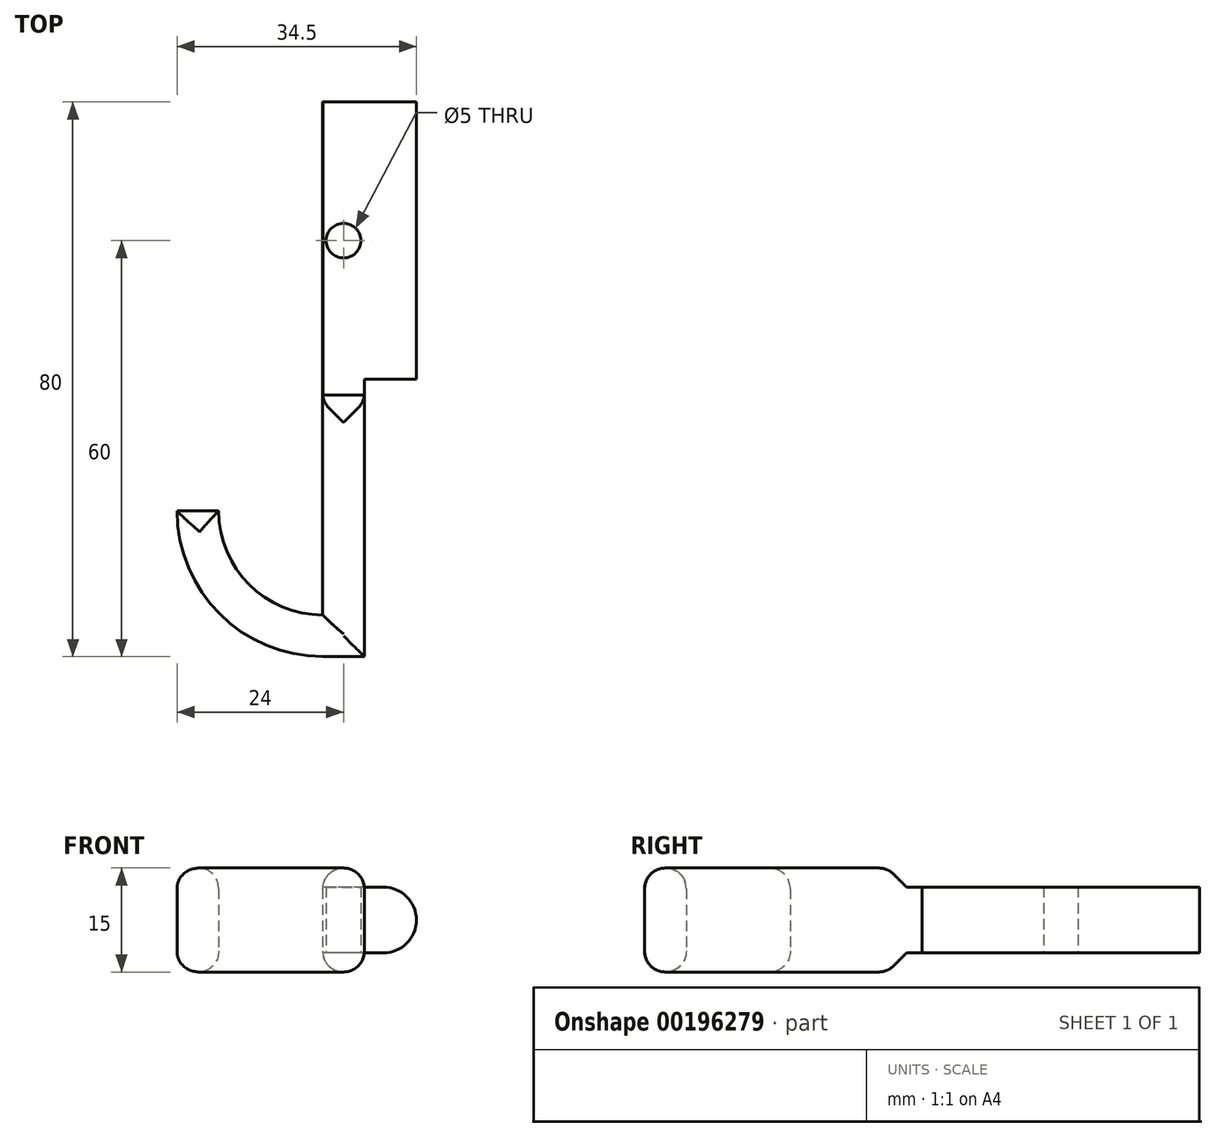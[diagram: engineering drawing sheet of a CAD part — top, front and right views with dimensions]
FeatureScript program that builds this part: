
annotation { "Feature Type Name" : "Feature", "Feature Type Description" : "" }
export const myFeature = defineFeature(function(context is Context, id is Id, definition is map)
    precondition{}
    {
        {
            var Q0;
            Q0=qCreatedBy(makeId("Top.planeOp"),FACE);
            var sketch = newSketch(context, id + "F0", { "sketchPlane" : qUnion([Q0])});
            skArc(sketch, "E0", {"start": v(0, -21) * mm, "mid": v(-14.85, -14.85) * mm, "end": v(-21, 0) * mm});
            skLineSegment(sketch, "E1", {"start": v(0, 0) * mm, "end": v(0, -15) * mm, "construction": true});
            skArc(sketch, "E2", {"start": v(0, -15) * mm, "mid": v(-10.6, -10.6) * mm, "end": v(-15, 0) * mm});
            skLineSegment(sketch, "E3", {"start": v(-21, 0) * mm, "end": v(-15, 0) * mm});
            skLineSegment(sketch, "E4", {"start": v(0, 0) * mm, "end": v(0, -21) * mm});
            skLineSegment(sketch, "E5.bottom", {"start": v(0, -21) * mm, "end": v(6, -21) * mm});
            skLineSegment(sketch, "E5.top", {"start": v(0, 19) * mm, "end": v(6, 19) * mm});
            skLineSegment(sketch, "E5.left", {"start": v(0, -21) * mm, "end": v(0, 19) * mm});
            skLineSegment(sketch, "E5.right", {"start": v(6, -21) * mm, "end": v(6, 19) * mm});
            skSolve(sketch);
        }
        {
            var Q0;
            Q0=qSketchRegion(id+"F0",true);
            extrude(context, id + "F1", {"entities" : qUnion([Q0]), "depth" : 15 * mm});
        }
        {
            var Q0;
            Q0=makeQuery(id+"F1.opExtrude","SWEPT_FACE",FACE,{"disambiguationData":[OSD([sQuery(id+"F0.wireOp",EDGE,"E5.top")])]});
            var sketch = newSketch(context, id + "F2", { "sketchPlane" : qUnion([Q0])});
            skLineSegment(sketch, "E6", {"start": v(-6, 15) * mm, "end": v(0, 0) * mm, "construction": true});
            skLineSegment(sketch, "E7", {"start": v(0, 0) * mm, "end": v(-6, 0) * mm, "construction": true});
            skLineSegment(sketch, "E8", {"start": v(-6, 0) * mm, "end": v(0, 15) * mm, "construction": true});
            skPoint(sketch, "E9", {"position": v(-3, 7.5) * mm});
            skLineSegment(sketch, "E10", {"start": v(-3, 7.5) * mm, "end": v(-3, 41.48) * mm, "construction": true});
            skLineSegment(sketch, "E11", {"start": v(-3, 7.5) * mm, "end": v(-3, -27.06) * mm, "construction": true});
            skLineSegment(sketch, "E12.bottom", {"start": v(-8.75, 2.75) * mm, "end": v(2.75, 2.75) * mm, "construction": true});
            skLineSegment(sketch, "E12.left", {"start": v(-8.75, 2.75) * mm, "end": v(-8.75, 12.25) * mm, "construction": true});
            skLineSegment(sketch, "E12.right", {"start": v(2.75, 2.75) * mm, "end": v(2.75, 12.25) * mm, "construction": true});
            skLineSegment(sketch, "E13", {"start": v(-3, 7.5) * mm, "end": v(-14.99, 7.5) * mm, "construction": true});
            skLineSegment(sketch, "E14", {"start": v(-14.99, 7.5) * mm, "end": v(-3, 7.5) * mm, "construction": true});
            skLineSegment(sketch, "E15", {"start": v(5.8, 7.5) * mm, "end": v(-3, 7.5) * mm, "construction": true});
            skPoint(sketch, "E16", {"position": v(-8.75, 7.5) * mm});
            skPoint(sketch, "E17", {"position": v(2.75, 7.5) * mm});
            skCircle(sketch, "E18", {"center": v(2.75, 7.5) * mm, "radius": 4.75 * mm, "construction": true});
            skCircle(sketch, "E19", {"center": v(-8.75, 7.5) * mm, "radius": 4.75 * mm, "construction": true});
            skLineSegment(sketch, "E20", {"start": v(2.75, 12.25) * mm, "end": v(-8.75, 12.25) * mm, "construction": true});
            skLineSegment(sketch, "E21", {"start": v(-8.75, 2.75) * mm, "end": v(2.75, 2.75) * mm});
            skArc(sketch, "E22", {"start": v(2.75, 12.25) * mm, "mid": v(7.5, 7.5) * mm, "end": v(2.75, 2.75) * mm});
            skArc(sketch, "E23", {"start": v(-8.75, 12.25) * mm, "mid": v(-13.5, 7.5) * mm, "end": v(-8.75, 2.75) * mm});
            skLineSegment(sketch, "E24", {"start": v(-8.75, 12.25) * mm, "end": v(2.75, 12.25) * mm});
            skSolve(sketch);
        }
        {
            var Q0;
            {var subQ0=sQuery(id+"F2.wireOp",EDGE,"E23");Q0=makeQuery(id+"F2.imprint","IMPRINT",FACE,{"disambiguationData":[TD([[makeQuery(id+"F2.imprint","IMPRINT",EDGE,{"derivedFrom":subQ0}),1.0]])]});}
            var Q1;
            {var subQ0=sQuery(id+"F2.wireOp",EDGE,"E22");Q1=makeQuery(id+"F2.imprint","IMPRINT",FACE,{"disambiguationData":[TD([[makeQuery(id+"F2.imprint","IMPRINT",EDGE,{"derivedFrom":subQ0}),-1.0]])]});}
            var Q2;
            {var subQ0=sQuery(id+"F2.wireOp",EDGE,"E21");var subQ1=sQuery(id+"F0.wireOp",EDGE,"E5.top");var subQ2=makeQuery(id+"F1.opExtrude","SWEPT_EDGE",EDGE,{"disambiguationData":[OSD([subQ1,sQuery(id+"F0.wireOp",EDGE,"E5.right")])]});var subQ3=makeQuery(id+"F2.imprint","INTERSECT",VERTEX,{"derivedFrom":[subQ2,subQ0]});Q2=makeQuery(id+"F2.imprint","IMPRINT",FACE,{"disambiguationData":[TD([[makeQuery(id+"F2.imprint","IMPRINT",EDGE,{"disambiguationData":[TD([[subQ3,-1.0]])],"derivedFrom":subQ0}),1.0]])]});}
            extrude(context, id + "F3", {"entities" : qUnion([Q0, Q1, Q2]), "operationType" : NewBodyOperationType.ADD, "depth" : 40 * mm});
        }
        {
            var Q0;
            Q0=makeQuery(id+"F3.opExtrude","SWEPT_FACE",FACE,{"disambiguationData":[OSD([sQuery(id+"F2.wireOp",EDGE,"E24")])]});
            var sketch = newSketch(context, id + "F4", { "sketchPlane" : qUnion([Q0])});
            skLineSegment(sketch, "E25", {"start": v(-2.75, 59) * mm, "end": v(8.75, 19) * mm, "construction": true});
            skLineSegment(sketch, "E26", {"start": v(8.75, 19) * mm, "end": v(8.75, 59) * mm, "construction": true});
            skLineSegment(sketch, "E27", {"start": v(8.75, 59) * mm, "end": v(-2.75, 19) * mm, "construction": true});
            skPoint(sketch, "E28", {"position": v(3, 39) * mm});
            skSolve(sketch);
        }
        {
            var Q0;
            Q0=sQuery(id+"F4.wireOp",VERTEX,"E28");
            var Q1;
            Q1=makeQuery(id+"F1.opExtrude","SWEPT_BODY",BODY,{"disambiguationData":[OSD([sQuery(id+"F0.wireOp",EDGE,"E0"),sQuery(id+"F0.wireOp",EDGE,"E2"),sQuery(id+"F0.wireOp",EDGE,"E3"),sQuery(id+"F0.wireOp",EDGE,"E5.bottom"),sQuery(id+"F0.wireOp",EDGE,"E5.top"),sQuery(id+"F0.wireOp",EDGE,"E5.left"),sQuery(id+"F0.wireOp",EDGE,"E5.right")])]});
            hole(context, id + "F5", {"style" : HoleStyle.SIMPLE, "endStyle" : HoleEndStyle.THROUGH, "holeDiameter" : 5 * mm, "locations" : qUnion([Q0]), "scope" : qUnion([Q1]), "isTappedThrough" : true});
        }
        {
            var Q0;
            Q0=makeQuery(id+"F1.opExtrude","CAP_EDGE",EDGE,{"disambiguationData":[OSD([sQuery(id+"F0.wireOp",EDGE,"E5.top")])],"isStart":false});
            var Q1;
            Q1=makeQuery(id+"F1.opExtrude","CAP_EDGE",EDGE,{"disambiguationData":[OSD([sQuery(id+"F0.wireOp",EDGE,"E5.top")])],"isStart":true});
            chamfer(context, id + "F6", {"entities" : qUnion([Q0, Q1]), "width" : 5 * mm, "tangentPropagation" : true});
        }
        {
            var Q0;
            Q0=makeQuery(id+"F1.opExtrude","CAP_FACE",FACE,{"disambiguationData":[OSD([sQuery(id+"F0.wireOp",EDGE,"E0"),sQuery(id+"F0.wireOp",EDGE,"E2"),sQuery(id+"F0.wireOp",EDGE,"E3"),sQuery(id+"F0.wireOp",EDGE,"E5.bottom"),sQuery(id+"F0.wireOp",EDGE,"E5.top"),sQuery(id+"F0.wireOp",EDGE,"E5.left"),sQuery(id+"F0.wireOp",EDGE,"E5.right")])],"isStart":true});
            var Q1;
            Q1=makeQuery(id+"F1.opExtrude","CAP_FACE",FACE,{"disambiguationData":[OSD([sQuery(id+"F0.wireOp",EDGE,"E0"),sQuery(id+"F0.wireOp",EDGE,"E2"),sQuery(id+"F0.wireOp",EDGE,"E3"),sQuery(id+"F0.wireOp",EDGE,"E5.bottom"),sQuery(id+"F0.wireOp",EDGE,"E5.top"),sQuery(id+"F0.wireOp",EDGE,"E5.left"),sQuery(id+"F0.wireOp",EDGE,"E5.right")])],"isStart":false});
            fillet(context, id + "F7", {"entities" : qUnion([Q0, Q1]), "radius" : 3 * mm, "tangentPropagation" : true, "allowEdgeOverflow" : false});
        }
    });
